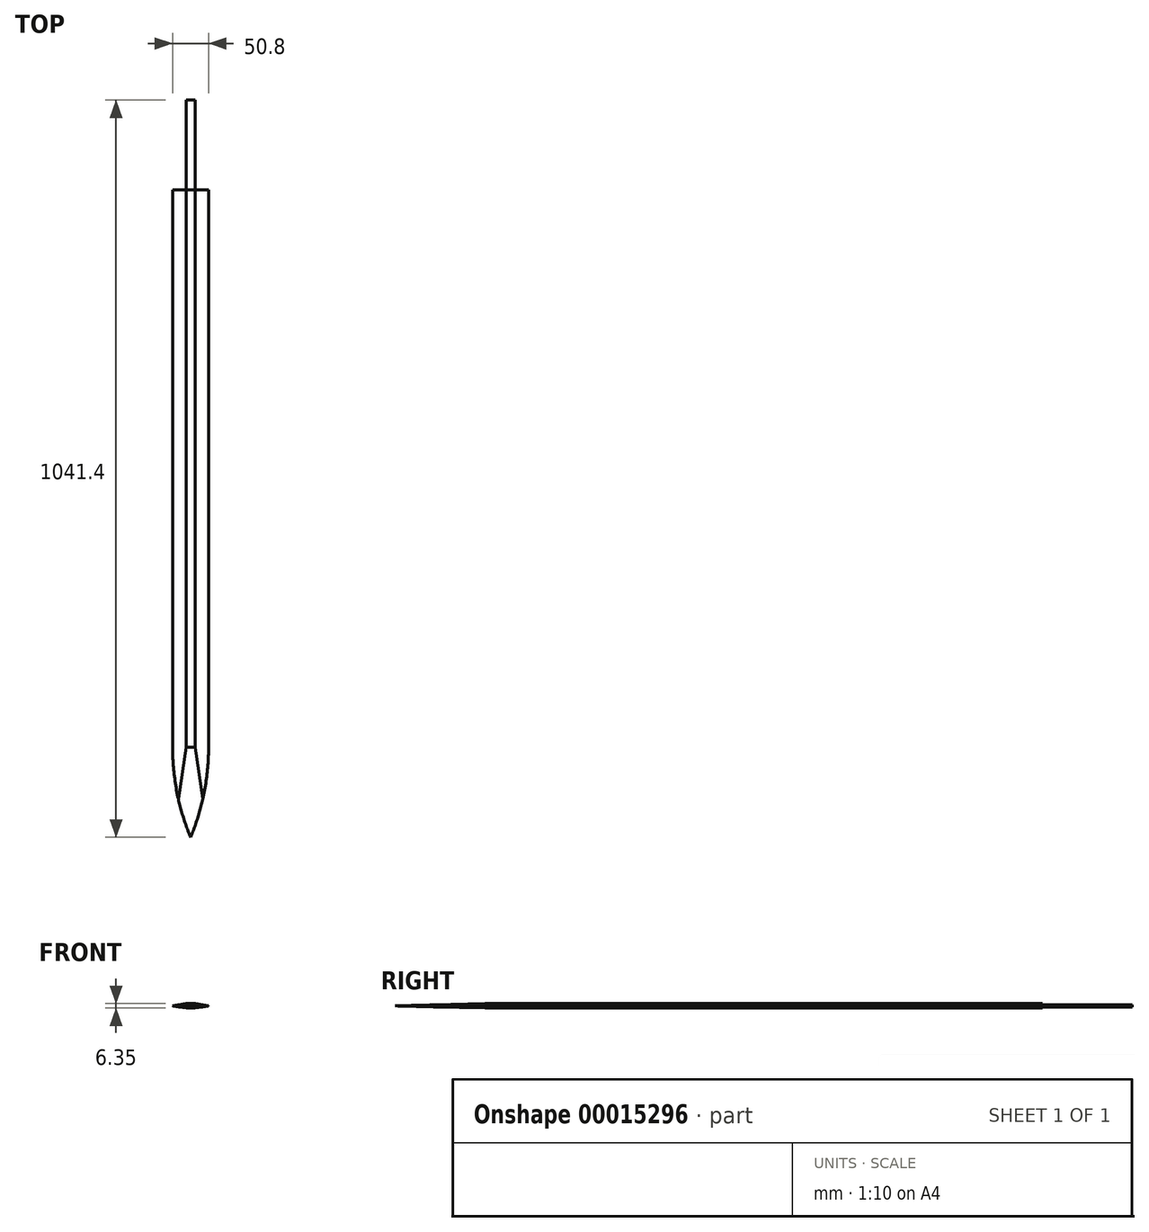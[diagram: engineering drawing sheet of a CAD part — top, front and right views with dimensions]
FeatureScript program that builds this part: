
annotation { "Feature Type Name" : "Feature", "Feature Type Description" : "" }
export const myFeature = defineFeature(function(context is Context, id is Id, definition is map)
    precondition{}
    {
        {
            var Q0;
            Q0=qCreatedBy(makeId("Top.planeOp"),FACE);
            var sketch = newSketch(context, id + "F0", { "sketchPlane" : qUnion([Q0])});
            skLineSegment(sketch, "E0.bottom", {"start": v(-202.3, 458.47) * mm, "end": v(-151.5, 458.47) * mm});
            skLineSegment(sketch, "E0.top", {"start": v(-202.3, -455.93) * mm, "end": v(-151.5, -455.93) * mm});
            skLineSegment(sketch, "E0.left", {"start": v(-202.3, 458.47) * mm, "end": v(-202.3, -455.93) * mm});
            skLineSegment(sketch, "E0.right", {"start": v(-151.5, 458.47) * mm, "end": v(-151.5, -455.93) * mm});
            skSolve(sketch);
        }
        {
            var Q0;
            Q0=makeQuery(id+"F0.imprint","IMPRINT",FACE,{"disambiguationData":[TD([[makeQuery(id+"F0.imprint","IMPRINT",EDGE,{"derivedFrom":sQuery(id+"F0.wireOp",EDGE,"E0.bottom")}),-1.0]])]});
            extrude(context, id + "F1", {"entities" : qUnion([Q0]), "depth" : 6.35 * mm});
        }
        {
            var Q0;
            Q0=makeQuery(id+"F1.opExtrude","SWEPT_FACE",FACE,{"disambiguationData":[OSD([sQuery(id+"F0.wireOp",EDGE,"E0.bottom")])]});
            var sketch = newSketch(context, id + "F2", { "sketchPlane" : qUnion([Q0])});
            skLineSegment(sketch, "E1", {"start": v(176.9, 6.35) * mm, "end": v(176.9, 0) * mm, "construction": true});
            skLineSegment(sketch, "E2", {"start": v(151.5, 3.18) * mm, "end": v(202.3, 3.18) * mm, "construction": true});
            skLineSegment(sketch, "E3", {"start": v(170.55, 6.35) * mm, "end": v(170.55, 0) * mm, "construction": true});
            skLineSegment(sketch, "E4", {"start": v(183.25, 6.35) * mm, "end": v(183.25, 0) * mm, "construction": true});
            skArc(sketch, "E5", {"start": v(170.55, 6.35) * mm, "mid": v(176.9, 4.76) * mm, "end": v(183.25, 6.35) * mm});
            skArc(sketch, "E6", {"start": v(183.25, 0) * mm, "mid": v(176.9, 1.59) * mm, "end": v(170.55, 0) * mm});
            skLineSegment(sketch, "E7", {"start": v(170.55, 6.35) * mm, "end": v(151.5, 3.18) * mm});
            skLineSegment(sketch, "E8", {"start": v(170.55, 0) * mm, "end": v(151.5, 3.18) * mm});
            skLineSegment(sketch, "E9", {"start": v(183.25, 0) * mm, "end": v(202.3, 3.18) * mm});
            skLineSegment(sketch, "E10", {"start": v(183.25, 6.35) * mm, "end": v(202.3, 3.18) * mm});
            skSolve(sketch);
        }
        {
            var Q0;
            Q0=makeQuery(id+"F1.opExtrude","SWEPT_FACE",FACE,{"disambiguationData":[OSD([sQuery(id+"F0.wireOp",EDGE,"E0.left")])]});
            var sketch = newSketch(context, id + "F3", { "sketchPlane" : qUnion([Q0])});
            skLineSegment(sketch, "E11", {"start": v(328.93, 0) * mm, "end": v(328.93, 6.35) * mm, "construction": true});
            skLineSegment(sketch, "E12", {"start": v(328.93, 6.35) * mm, "end": v(455.93, 3.18) * mm});
            skLineSegment(sketch, "E13", {"start": v(455.93, 3.18) * mm, "end": v(328.93, 0) * mm});
            skSolve(sketch);
        }
        {
            var Q0;
            {var subQ2=sQuery(id+"F3.wireOp",EDGE,"E12");Q0=makeQuery(id+"F3.imprint","IMPRINT",FACE,{"disambiguationData":[TD([[makeQuery(id+"F3.imprint","IMPRINT",EDGE,{"derivedFrom":subQ2}),1.0]])]});}
            var Q1;
            {var subQ2=sQuery(id+"F3.wireOp",EDGE,"E13");Q1=makeQuery(id+"F3.imprint","IMPRINT",FACE,{"disambiguationData":[TD([[makeQuery(id+"F3.imprint","IMPRINT",EDGE,{"derivedFrom":subQ2}),1.0]])]});}
            extrude(context, id + "F4", {"entities" : qUnion([Q0, Q1]), "operationType" : NewBodyOperationType.REMOVE, "oppositeDirection" : true, "depth" : 96 * mm});
        }
        {
            var Q0;
            Q0=makeQuery(id+"F4.boolean.opBoolean","COPY",FACE,{"derivedFrom":makeQuery(id+"F4.opExtrude","SWEPT_FACE",FACE,{"disambiguationData":[OSD([sQuery(id+"F3.wireOp",EDGE,"E12")])]})});
            var sketch = newSketch(context, id + "F5", { "sketchPlane" : qUnion([Q0])});
            skArc(sketch, "E14", {"start": v(-202.3, -328.67) * mm, "mid": v(-195.89, -393.45) * mm, "end": v(-176.9, -455.7) * mm});
            skArc(sketch, "E15", {"start": v(-176.9, -455.7) * mm, "mid": v(-157.91, -393.45) * mm, "end": v(-151.5, -328.67) * mm});
            skSolve(sketch);
        }
        {
            var Q0;
            {var subQ5=sQuery(id+"F5.wireOp",EDGE,"E14");Q0=makeQuery(id+"F5.imprint","IMPRINT",FACE,{"disambiguationData":[TD([[makeQuery(id+"F5.imprint","IMPRINT",EDGE,{"derivedFrom":subQ5}),-1.0]])]});}
            var Q1;
            {var subQ5=sQuery(id+"F5.wireOp",EDGE,"E15");Q1=makeQuery(id+"F5.imprint","IMPRINT",FACE,{"disambiguationData":[TD([[makeQuery(id+"F5.imprint","IMPRINT",EDGE,{"derivedFrom":subQ5}),-1.0]])]});}
            extrude(context, id + "F6", {"entities" : qUnion([Q0, Q1]), "operationType" : NewBodyOperationType.REMOVE, "oppositeDirection" : true, "depth" : 25.4 * mm});
        }
        {
            var Q0;
            {var subQ2=sQuery(id+"F2.wireOp",EDGE,"E10");Q0=makeQuery(id+"F2.imprint","IMPRINT",FACE,{"disambiguationData":[TD([[makeQuery(id+"F2.imprint","IMPRINT",EDGE,{"derivedFrom":subQ2}),1.0]])]});}
            var Q1;
            {var subQ2=sQuery(id+"F2.wireOp",EDGE,"E9");Q1=makeQuery(id+"F2.imprint","IMPRINT",FACE,{"disambiguationData":[TD([[makeQuery(id+"F2.imprint","IMPRINT",EDGE,{"derivedFrom":subQ2}),-1.0]])]});}
            var Q2;
            {var subQ2=sQuery(id+"F2.wireOp",EDGE,"E7");Q2=makeQuery(id+"F2.imprint","IMPRINT",FACE,{"disambiguationData":[TD([[makeQuery(id+"F2.imprint","IMPRINT",EDGE,{"derivedFrom":subQ2}),-1.0]])]});}
            var Q3;
            {var subQ2=sQuery(id+"F2.wireOp",EDGE,"E8");Q3=makeQuery(id+"F2.imprint","IMPRINT",FACE,{"disambiguationData":[TD([[makeQuery(id+"F2.imprint","IMPRINT",EDGE,{"derivedFrom":subQ2}),1.0]])]});}
            extrude(context, id + "F7", {"entities" : qUnion([Q0, Q1, Q2, Q3]), "operationType" : NewBodyOperationType.REMOVE, "oppositeDirection" : true, "depth" : 915.77 * mm});
        }
        {
            var Q0;
            {var subQ1=sQuery(id+"F2.wireOp",EDGE,"E5");Q0=makeQuery(id+"F2.imprint","IMPRINT",FACE,{"disambiguationData":[TD([[makeQuery(id+"F2.imprint","IMPRINT",EDGE,{"derivedFrom":subQ1}),1.0]])]});}
            var Q1;
            {var subQ1=sQuery(id+"F2.wireOp",EDGE,"E6");Q1=makeQuery(id+"F2.imprint","IMPRINT",FACE,{"disambiguationData":[TD([[makeQuery(id+"F2.imprint","IMPRINT",EDGE,{"derivedFrom":subQ1}),1.0]])]});}
            extrude(context, id + "F8", {"entities" : qUnion([Q0, Q1]), "operationType" : NewBodyOperationType.REMOVE, "oppositeDirection" : true, "depth" : 787.4 * mm});
        }
        {
            var Q0;
            Q0=makeQuery(id+"F1.opExtrude","SWEPT_FACE",FACE,{"disambiguationData":[OSD([sQuery(id+"F0.wireOp",EDGE,"E0.bottom")])]});
            var sketch = newSketch(context, id + "F9", { "sketchPlane" : qUnion([Q0])});
            skLineSegment(sketch, "E16", {"start": v(170.55, 6.35) * mm, "end": v(170.55, 0) * mm});
            skLineSegment(sketch, "E17", {"start": v(170.55, 0) * mm, "end": v(183.25, 0) * mm});
            skLineSegment(sketch, "E18", {"start": v(183.25, 0) * mm, "end": v(183.25, 6.35) * mm});
            skLineSegment(sketch, "E19", {"start": v(183.25, 6.35) * mm, "end": v(170.55, 6.35) * mm});
            skLineSegment(sketch, "E20", {"start": v(202.3, 3.18) * mm, "end": v(151.5, 3.18) * mm, "construction": true});
            skSolve(sketch);
        }
        {
            var Q0;
            Q0=makeQuery(id+"F9.imprint","IMPRINT",FACE,{"disambiguationData":[TD([[makeQuery(id+"F9.imprint","IMPRINT",EDGE,{"derivedFrom":sQuery(id+"F9.wireOp",EDGE,"E16")}),1.0]])]});
            var Q1;
            Q1=makeQuery(id+"F9.imprint","IMPRINT",FACE,{"disambiguationData":[TD([[makeQuery(id+"F9.imprint","IMPRINT",EDGE,{"derivedFrom":sQuery(id+"F9.wireOp",EDGE,"E19")}),1.0]])]});
            var Q2;
            Q2=makeQuery(id+"F9.imprint","IMPRINT",FACE,{"disambiguationData":[TD([[makeQuery(id+"F9.imprint","IMPRINT",EDGE,{"derivedFrom":sQuery(id+"F9.wireOp",EDGE,"E17")}),1.0]])]});
            extrude(context, id + "F10", {"entities" : qUnion([Q0, Q1, Q2]), "operationType" : NewBodyOperationType.ADD, "depth" : 127 * mm});
        }
        {
            var Q0;
            Q0=makeQuery(id+"F10.opExtrude","SWEPT_FACE",FACE,{"disambiguationData":[OSD([sQuery(id+"F9.wireOp",EDGE,"E16")])]});
            var sketch = newSketch(context, id + "F11", { "sketchPlane" : qUnion([Q0])});
            skSolve(sketch);
        }
        {
            var Q0;
            Q0 = qSketchRegion(id + "F11", true);
            var Q1;
            Q1=makeQuery(id+"F10.opExtrude","SWEPT_FACE",FACE,{"disambiguationData":[OSD([sQuery(id+"F9.wireOp",EDGE,"E19")])]});
            extrude(context, id + "F12", {"entities" : qUnion([Q0, Q1]), "operationType" : NewBodyOperationType.REMOVE, "oppositeDirection" : true, "depth" : 1.78 * mm});
        }
        {
            var Q0;
            Q0=makeQuery(id+"F10.opExtrude","SWEPT_FACE",FACE,{"disambiguationData":[OSD([sQuery(id+"F9.wireOp",EDGE,"E17")])]});
            extrude(context, id + "F13", {"entities" : qUnion([Q0]), "operationType" : NewBodyOperationType.REMOVE, "oppositeDirection" : true, "depth" : 1.78 * mm});
        }
    });
